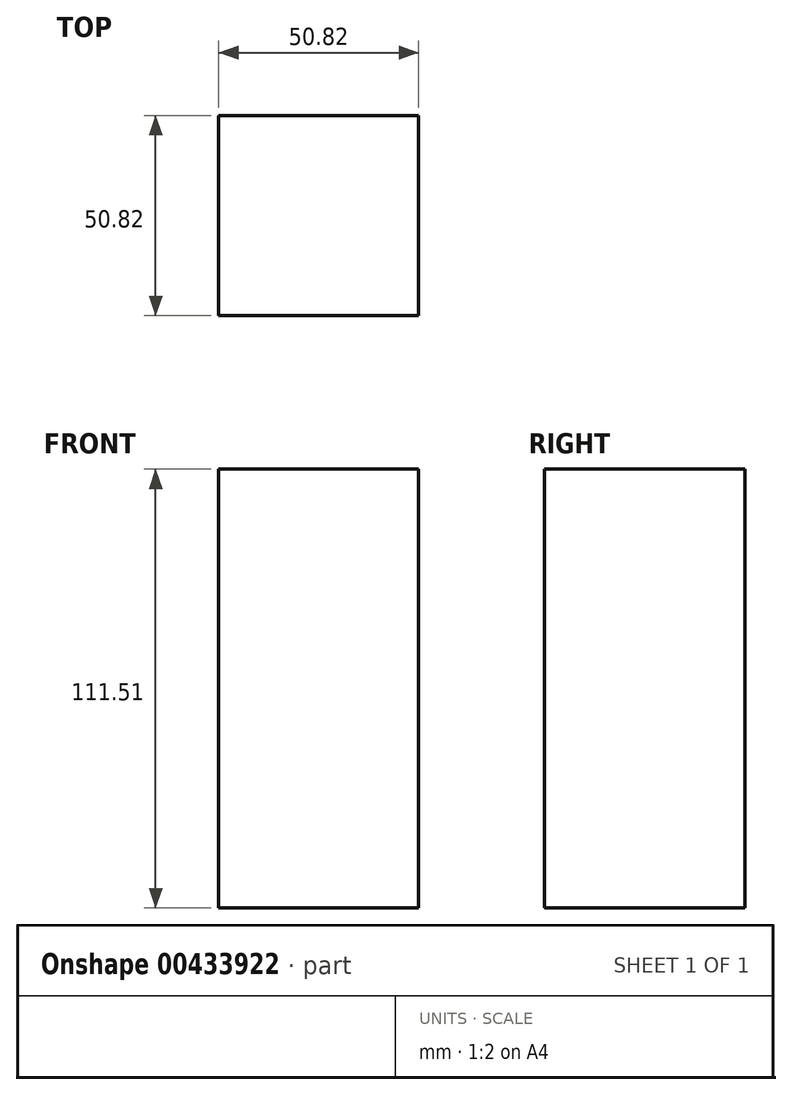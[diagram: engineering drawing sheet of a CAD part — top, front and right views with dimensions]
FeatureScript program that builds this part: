
annotation { "Feature Type Name" : "Feature", "Feature Type Description" : "" }
export const myFeature = defineFeature(function(context is Context, id is Id, definition is map)
    precondition{}
    {
        {
            var Q0;
            Q0=qCreatedBy(makeId("Top.planeOp"),FACE);
            var sketch = newSketch(context, id + "F0", { "sketchPlane" : qUnion([Q0])});
            skLineSegment(sketch, "E0.bottom", {"start": v(-25.4, -25.4) * mm, "end": v(25.4, -25.4) * mm});
            skLineSegment(sketch, "E0.top", {"start": v(-25.4, 25.4) * mm, "end": v(25.4, 25.4) * mm});
            skLineSegment(sketch, "E0.left", {"start": v(-25.4, -25.4) * mm, "end": v(-25.4, 25.4) * mm});
            skLineSegment(sketch, "E0.right", {"start": v(25.4, -25.4) * mm, "end": v(25.4, 25.4) * mm});
            skPoint(sketch, "E0.middle", {"position": v(0, 0) * mm});
            skSolve(sketch);
        }
        {
            var Q0;
            Q0 = qSketchRegion(id + "F0", true);
            extrude(context, id + "F1", {"entities" : qUnion([Q0]), "depth" : 111.5 * mm});
        }
    });
